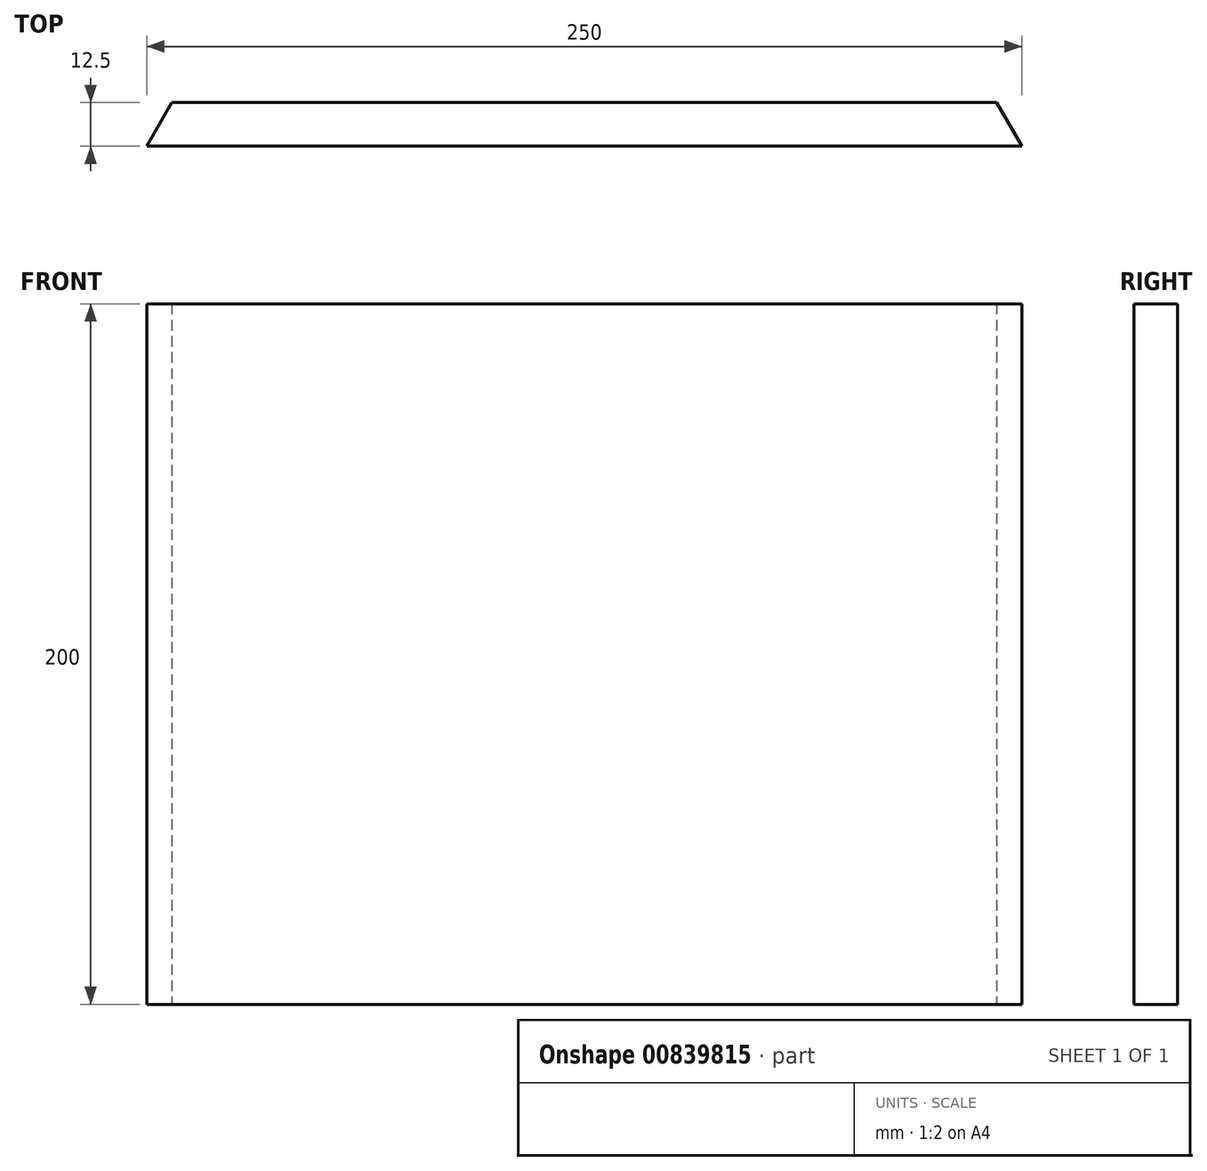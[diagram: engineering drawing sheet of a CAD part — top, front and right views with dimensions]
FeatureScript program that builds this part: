
annotation { "Feature Type Name" : "Feature", "Feature Type Description" : "" }
export const myFeature = defineFeature(function(context is Context, id is Id, definition is map)
    precondition{}
    {
        {
            var Q0;
            Q0=qCreatedBy(makeId("Top.planeOp"),FACE);
            var sketch = newSketch(context, id + "F0", { "sketchPlane" : qUnion([Q0])});
            skLineSegment(sketch, "E0.bottom", {"start": v(-130.63, -65.3) * mm, "end": v(104.93, -65.3) * mm});
            skLineSegment(sketch, "E0.top", {"start": v(-137.85, -77.8) * mm, "end": v(112.15, -77.8) * mm});
            skLineSegment(sketch, "E1", {"start": v(-137.85, -77.8) * mm, "end": v(-130.63, -65.3) * mm});
            skLineSegment(sketch, "E2", {"start": v(112.15, -77.8) * mm, "end": v(104.93, -65.3) * mm});
            skSolve(sketch);
        }
        {
            var Q0;
            Q0=makeQuery(id+"F0.imprint","IMPRINT",FACE,{"disambiguationData":[TD([[makeQuery(id+"F0.imprint","IMPRINT",EDGE,{"derivedFrom":sQuery(id+"F0.wireOp",EDGE,"E0.bottom")}),-1.0]])]});
            extrude(context, id + "F1", {"entities" : qUnion([Q0]), "depth" : 200 * mm, "offsetDistance" : 25 * mm});
        }
    });
